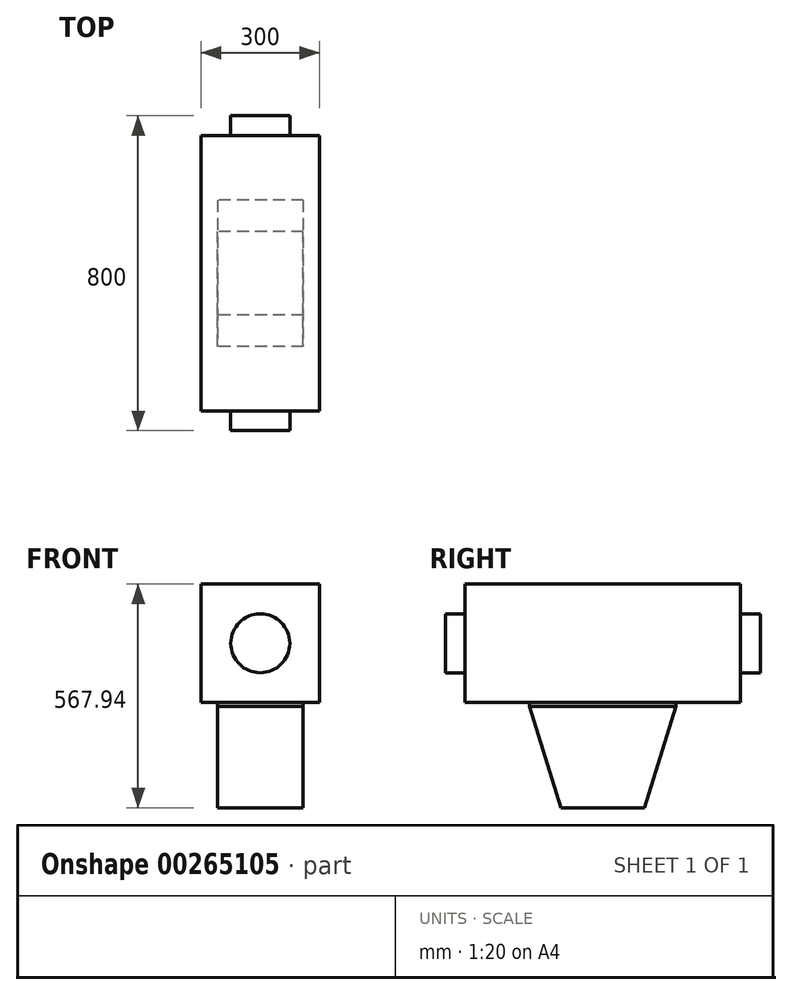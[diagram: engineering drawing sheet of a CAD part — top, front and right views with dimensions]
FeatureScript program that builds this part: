
annotation { "Feature Type Name" : "Feature", "Feature Type Description" : "" }
export const myFeature = defineFeature(function(context is Context, id is Id, definition is map)
    precondition{}
    {
        {
            var Q0;
            Q0=qCreatedBy(makeId("Right.planeOp"),FACE);
            var sketch = newSketch(context, id + "F0", { "sketchPlane" : qUnion([Q0])});
            skLineSegment(sketch, "E0.bottom", {"start": v(350, 150) * mm, "end": v(-350, 150) * mm});
            skLineSegment(sketch, "E0.top", {"start": v(350, -150) * mm, "end": v(-350, -150) * mm});
            skLineSegment(sketch, "E0.left", {"start": v(350, 150) * mm, "end": v(350, -150) * mm});
            skLineSegment(sketch, "E0.right", {"start": v(-350, 150) * mm, "end": v(-350, -150) * mm});
            skPoint(sketch, "E0.middle", {"position": v(0, 0) * mm});
            skLineSegment(sketch, "E1", {"start": v(350, 0) * mm, "end": v(350, 75) * mm});
            skSolve(sketch);
        }
        {
            var Q0;
            Q0 = qSketchRegion(id + "F0", true);
            extrude(context, id + "F1", {"entities" : qUnion([Q0]), "depth" : 300 * mm});
        }
        {
            var Q0;
            Q0=makeQuery(id+"F1.opExtrude","SWEPT_FACE",FACE,{"disambiguationData":[OSD([sQuery(id+"F0.wireOp",EDGE,"E0.left"),sQuery(id+"F0.wireOp",EDGE,"E1")])]});
            var sketch = newSketch(context, id + "F2", { "sketchPlane" : qUnion([Q0])});
            skCircle(sketch, "E2", {"center": v(-150, 0) * mm, "radius": 75 * mm});
            skPoint(sketch, "E2.centerSnap0", {"position": v(-150, 150) * mm});
            skSolve(sketch);
        }
        {
            var Q0;
            Q0 = qSketchRegion(id + "F2", true);
            extrude(context, id + "F3", {"entities" : qUnion([Q0]), "operationType" : NewBodyOperationType.ADD, "depth" : 50 * mm});
        }
        {
            var Q0;
            Q0=makeQuery(id+"F1.opExtrude","SWEPT_FACE",FACE,{"disambiguationData":[OSD([sQuery(id+"F0.wireOp",EDGE,"E0.top")])]});
            var sketch = newSketch(context, id + "F4", { "sketchPlane" : qUnion([Q0])});
            skLineSegment(sketch, "E3.bottom", {"start": v(41, -185.8) * mm, "end": v(259, -185.8) * mm});
            skLineSegment(sketch, "E3.top", {"start": v(41, 185.8) * mm, "end": v(259, 185.8) * mm});
            skLineSegment(sketch, "E3.left", {"start": v(41, -185.8) * mm, "end": v(41, 185.8) * mm});
            skLineSegment(sketch, "E3.right", {"start": v(259, -185.8) * mm, "end": v(259, 185.8) * mm});
            skPoint(sketch, "E3.middle", {"position": v(150, 0) * mm});
            skPoint(sketch, "E3.middle.positionSnap0", {"position": v(150, -350) * mm});
            skPoint(sketch, "E3.middle.positionSnap1", {"position": v(0, 0) * mm});
            skPoint(sketch, "E3.centerSnap0", {"position": v(150, -350) * mm});
            skPoint(sketch, "E3.centerSnap1", {"position": v(0, 0) * mm});
            skSolve(sketch);
        }
        {
            var Q0;
            Q0 = qSketchRegion(id + "F4", true);
            extrude(context, id + "F5", {"entities" : qUnion([Q0]), "operationType" : NewBodyOperationType.ADD, "depth" : 10 * mm});
        }
        {
            var Q0;
            Q0=makeQuery(id+"F5.opExtrude","SWEPT_FACE",FACE,{"disambiguationData":[OSD([sQuery(id+"F4.wireOp",EDGE,"E3.left")])]});
            var sketch = newSketch(context, id + "F6", { "sketchPlane" : qUnion([Q0])});
            skLineSegment(sketch, "E4", {"start": v(-185.8, -160) * mm, "end": v(-106, -417.94) * mm});
            skLineSegment(sketch, "E5", {"start": v(185.8, -160) * mm, "end": v(106, -417.94) * mm});
            skLineSegment(sketch, "E6", {"start": v(106, -417.94) * mm, "end": v(-106, -417.94) * mm});
            skSolve(sketch);
        }
        {
            var Q0;
            Q0=makeQuery(id+"F6.imprint","IMPRINT",FACE,{"disambiguationData":[TD([[makeQuery(id+"F6.imprint","IMPRINT",EDGE,{"derivedFrom":sQuery(id+"F6.wireOp",EDGE,"E4")}),1.0]])]});
            extrude(context, id + "F7", {"entities" : qUnion([Q0]), "oppositeDirection" : true, "depth" : 218 * mm});
        }
        {
            var Q0;
            Q0=makeQuery(id+"F1.opExtrude","SWEPT_FACE",FACE,{"disambiguationData":[OSD([sQuery(id+"F0.wireOp",EDGE,"E0.right")])]});
            var sketch = newSketch(context, id + "F8", { "sketchPlane" : qUnion([Q0])});
            skPoint(sketch, "E7.centerSnap0", {"position": v(150, 150) * mm});
            skCircle(sketch, "E8", {"center": v(150, 0) * mm, "radius": 75 * mm});
            skSolve(sketch);
        }
        {
            var Q0;
            Q0 = qSketchRegion(id + "F8", true);
            extrude(context, id + "F9", {"entities" : qUnion([Q0]), "operationType" : NewBodyOperationType.ADD, "depth" : 50 * mm});
        }
    });
